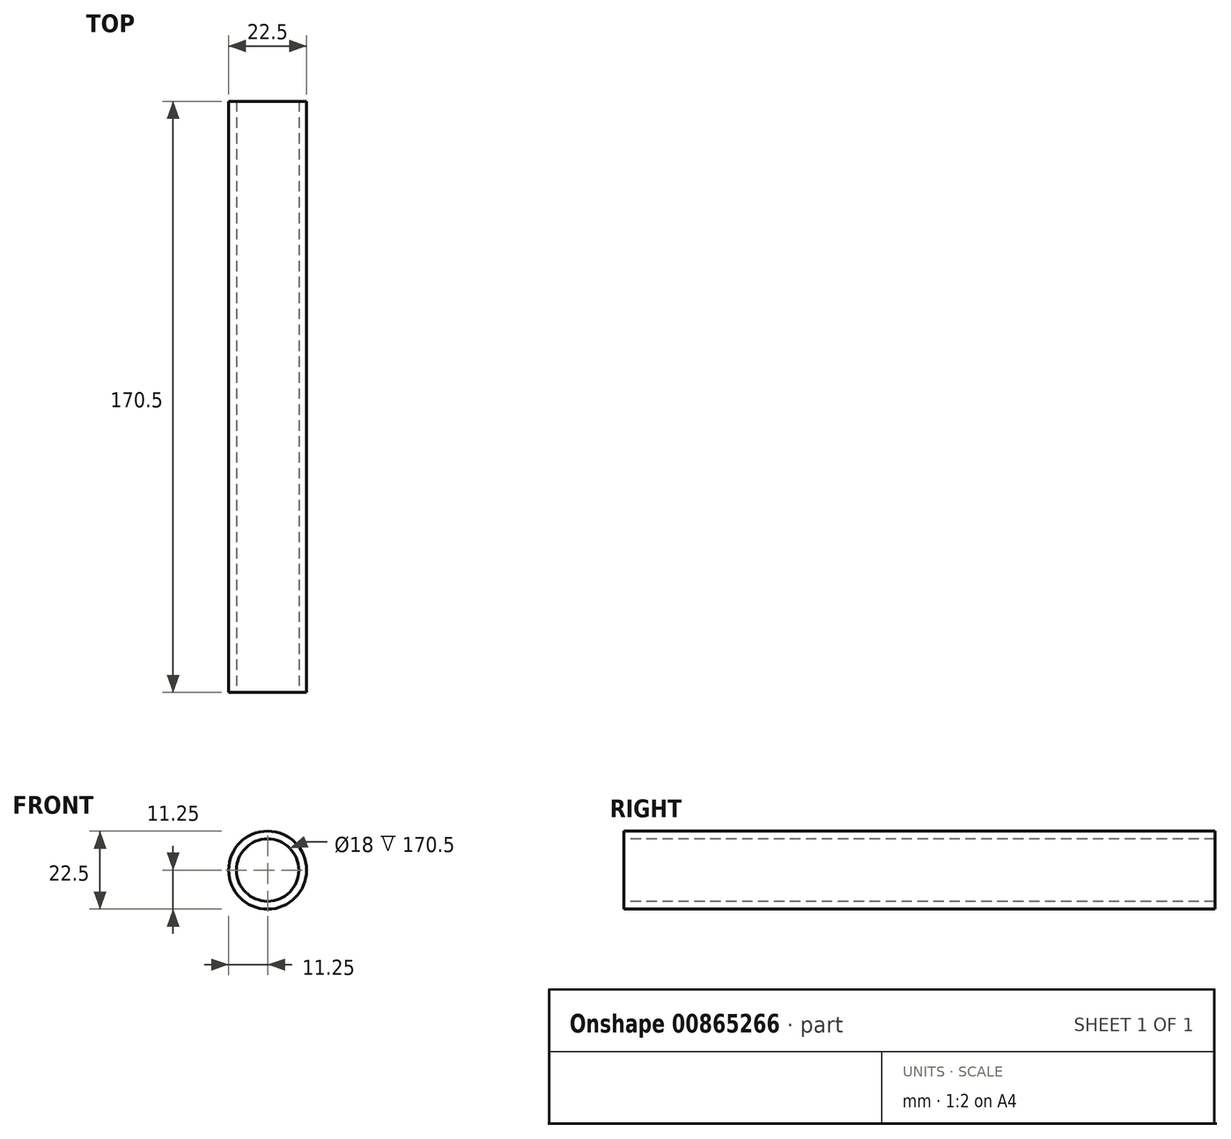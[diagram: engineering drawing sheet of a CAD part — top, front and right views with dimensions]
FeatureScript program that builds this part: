
annotation { "Feature Type Name" : "Feature", "Feature Type Description" : "" }
export const myFeature = defineFeature(function(context is Context, id is Id, definition is map)
    precondition{}
    {
        {
            var Q0;
            Q0=qCreatedBy(makeId("Front.planeOp"),FACE);
            var sketch = newSketch(context, id + "F0", { "sketchPlane" : qUnion([Q0])});
            skCircle(sketch, "E0", {"center": v(0, 0) * mm, "radius": 11.25 * mm});
            skCircle(sketch, "E1", {"center": v(0, 0) * mm, "radius": 9 * mm});
            skSolve(sketch);
        }
        {
            var Q0;
            Q0 = qSketchRegion(id + "F0", true);
            extrude(context, id + "F1", {"entities" : qUnion([Q0]), "oppositeDirection" : true, "depth" : 170.5 * mm, "offsetDistance" : 25 * mm});
        }
    });
